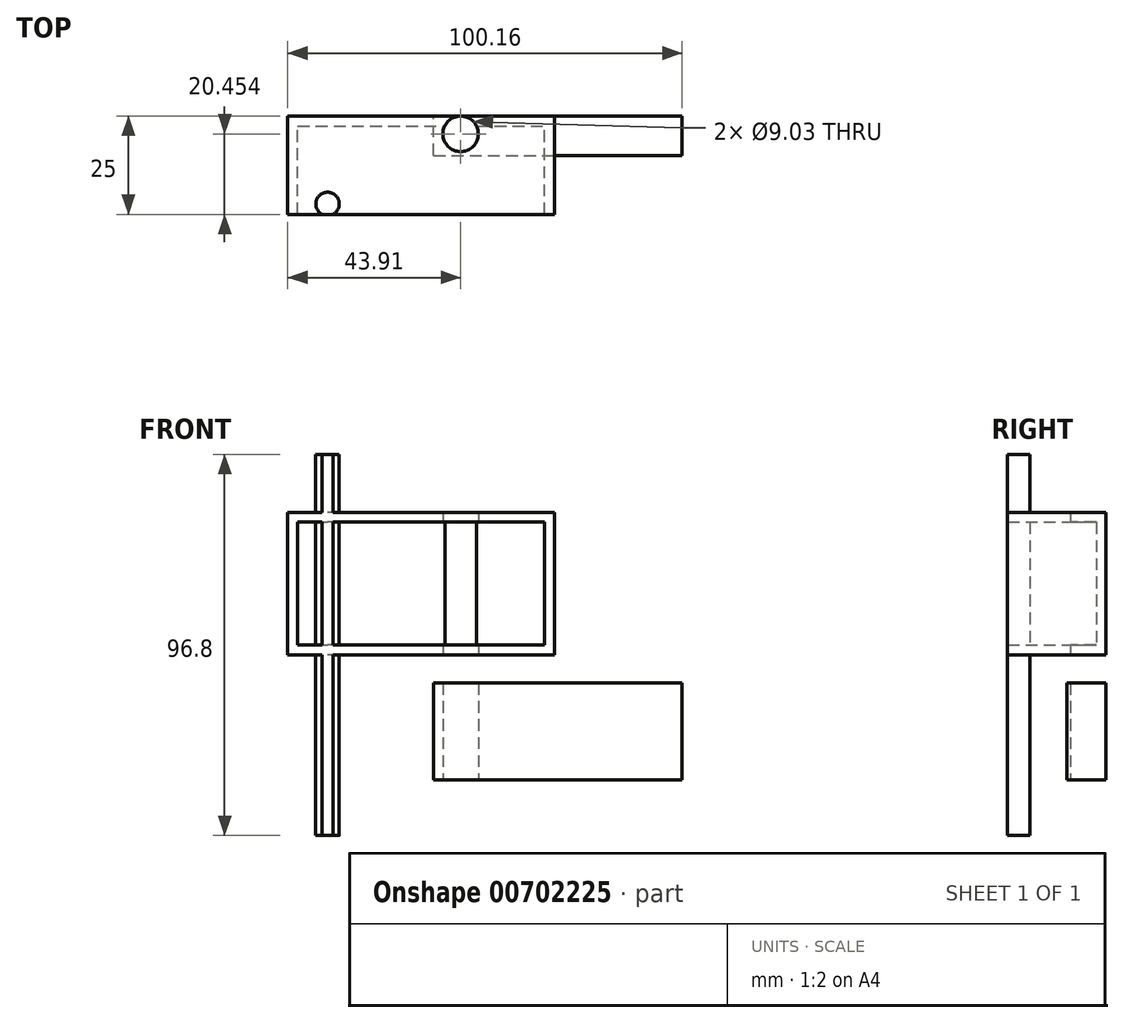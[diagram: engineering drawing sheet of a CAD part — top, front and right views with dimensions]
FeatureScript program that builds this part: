
annotation { "Feature Type Name" : "Feature", "Feature Type Description" : "" }
export const myFeature = defineFeature(function(context is Context, id is Id, definition is map)
    precondition{}
    {
        {
            var Q0;
            Q0=qCreatedBy(makeId("Front.planeOp"),FACE);
            var sketch = newSketch(context, id + "F0", { "sketchPlane" : qUnion([Q0])});
            skLineSegment(sketch, "E0.bottom", {"start": v(-39.38, 13.03) * mm, "end": v(28.4, 13.03) * mm});
            skLineSegment(sketch, "E0.top", {"start": v(-39.38, -23.19) * mm, "end": v(28.4, -23.19) * mm});
            skLineSegment(sketch, "E0.left", {"start": v(-39.38, 13.03) * mm, "end": v(-39.38, -23.19) * mm});
            skLineSegment(sketch, "E0.right", {"start": v(28.4, 13.03) * mm, "end": v(28.4, -23.19) * mm});
            skSolve(sketch);
        }
        {
            var Q0;
            Q0 = qSketchRegion(id + "F0", true);
            extrude(context, id + "F1", {"entities" : qUnion([Q0]), "depth" : 25 * mm, "offsetDistance" : 25 * mm});
        }
        {
            var Q0;
            Q0=makeQuery(id+"F1.opExtrude","CAP_FACE",FACE,{"disambiguationData":[OSD([sQuery(id+"F0.wireOp",EDGE,"E0.bottom"),sQuery(id+"F0.wireOp",EDGE,"E0.top"),sQuery(id+"F0.wireOp",EDGE,"E0.left"),sQuery(id+"F0.wireOp",EDGE,"E0.right")])],"isStart":false});
            shell(context, id + "F2", {"entities" : qUnion([Q0]), "thickness" : 2.5 * mm});
        }
        {
            var Q0;
            Q0=makeQuery(id+"F2.opShell","OFFSET_FACE",FACE,{"disambiguationData":[OSD([sQuery(id+"F0.wireOp",EDGE,"E0.top")])]});
            var sketch = newSketch(context, id + "F3", { "sketchPlane" : qUnion([Q0])});
            skCircle(sketch, "E1", {"center": v(-29.28, -22.34) * mm, "radius": 2.97 * mm});
            skSolve(sketch);
        }
        {
            var Q0;
            {var subQ0=sQuery(id+"F3.wireOp",EDGE,"E1");var subQ1=sQuery(id+"F0.wireOp",EDGE,"E0.top");var subQ2=makeQuery(id+"F2.opShell","OFFSET_EDGE",EDGE,{"disambiguationData":[OSD([subQ1]),TDD([makeQuery(id+"F1.opExtrude","CAP_EDGE",EDGE,{"disambiguationData":[OSD([subQ1])],"isStart":false})])]});var subQ3=makeQuery(id+"F3.imprint","INTERSECT",VERTEX,{"disambiguationData":[OD(0.0)],"derivedFrom":[subQ2,subQ0]});Q0=makeQuery(id+"F3.imprint","IMPRINT",FACE,{"disambiguationData":[TD([[makeQuery(id+"F3.imprint","IMPRINT",EDGE,{"disambiguationData":[TD([[subQ3,1.0]])],"derivedFrom":subQ0}),1.0]])]});}
            extrude(context, id + "F4", {"entities" : qUnion([Q0]), "operationType" : NewBodyOperationType.ADD, "endBound" : BoundingType.SYMMETRIC, "depth" : 96.8 * mm, "offsetDistance" : 25 * mm});
        }
        {
            var Q0;
            Q0=makeQuery(id+"F1.opExtrude","SWEPT_BODY",BODY,{"disambiguationData":[OSD([sQuery(id+"F0.wireOp",EDGE,"E0.bottom"),sQuery(id+"F0.wireOp",EDGE,"E0.top"),sQuery(id+"F0.wireOp",EDGE,"E0.left"),sQuery(id+"F0.wireOp",EDGE,"E0.right")])]});
            transform(context, id + "F5", {"entities" : qUnion([Q0]), "transformType" : TransformType.TRANSLATION_3D, "dx" : 0 * mm, "dy" : 0 * mm, "dz" : 0 * mm, "makeCopy" : true});
        }
        {
            var Q0;
            Q0=qCreatedBy(makeId("Front.planeOp"),FACE);
            var sketch = newSketch(context, id + "F6", { "sketchPlane" : qUnion([Q0])});
            skLineSegment(sketch, "E2.bottom", {"start": v(-2.33, -30.32) * mm, "end": v(60.78, -30.32) * mm});
            skLineSegment(sketch, "E2.top", {"start": v(-2.33, -55.02) * mm, "end": v(60.78, -55.02) * mm});
            skLineSegment(sketch, "E2.left", {"start": v(-2.33, -30.32) * mm, "end": v(-2.33, -55.02) * mm});
            skLineSegment(sketch, "E2.right", {"start": v(60.78, -30.32) * mm, "end": v(60.78, -55.02) * mm});
            skSolve(sketch);
        }
        {
            var Q0;
            Q0 = qSketchRegion(id + "F6", true);
            extrude(context, id + "F7", {"entities" : qUnion([Q0]), "depth" : 10 * mm, "offsetDistance" : 25 * mm});
        }
        {
            var Q0;
            Q0=makeQuery(id+"F5.opPattern","COPY",BODY,{"derivedFrom":makeQuery(id+"F1.opExtrude","SWEPT_BODY",BODY,{"disambiguationData":[OSD([sQuery(id+"F0.wireOp",EDGE,"E0.bottom"),sQuery(id+"F0.wireOp",EDGE,"E0.top"),sQuery(id+"F0.wireOp",EDGE,"E0.left"),sQuery(id+"F0.wireOp",EDGE,"E0.right")])]}),"instanceName":"1"});
            deleteBodies(context, id + "F8", {"entities" : qUnion([Q0])});
        }
        {
            var Q0;
            Q0=makeQuery(id+"F7.opExtrude","SWEPT_FACE",FACE,{"disambiguationData":[OSD([sQuery(id+"F6.wireOp",EDGE,"E2.top")])]});
            var sketch = newSketch(context, id + "F9", { "sketchPlane" : qUnion([Q0])});
            skCircle(sketch, "E3", {"center": v(4.53, 4.55) * mm, "radius": 4.51 * mm});
            skSolve(sketch);
        }
        {
            var Q0;
            Q0=makeQuery(id+"F9.imprint","IMPRINT",FACE,{"disambiguationData":[TD([[makeQuery(id+"F9.imprint","IMPRINT",EDGE,{"derivedFrom":sQuery(id+"F9.wireOp",EDGE,"E3")}),1.0]])]});
            extrude(context, id + "F10", {"entities" : qUnion([Q0]), "operationType" : NewBodyOperationType.REMOVE, "endBound" : BoundingType.THROUGH_ALL, "oppositeDirection" : true, "depth" : 20 * mm, "offsetDistance" : 25 * mm});
        }
    });
